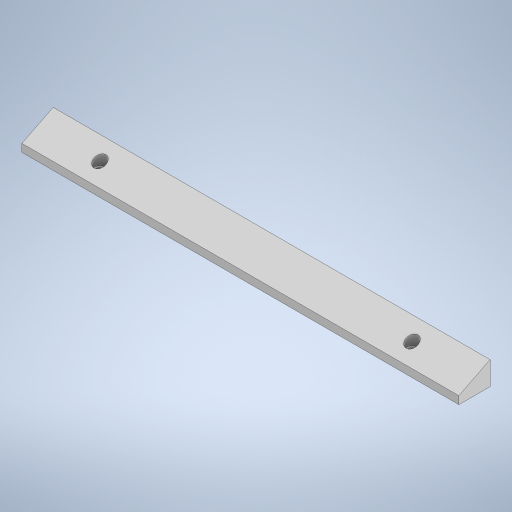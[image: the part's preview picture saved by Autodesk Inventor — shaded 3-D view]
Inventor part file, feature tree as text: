
AUTODESK INVENTOR PART (.ipt)
format: ipt  version: 2023 (Build 270158000, 158)  size: 270,848 bytes
history: native  units: in
note: dims shown in document units (in); Inventor stores cm internally (conversion verified against a paired STEP export)
features: sketch x6, extrude x5
ambient origin geometry x8: Origin, YZ Plane, XZ Plane, XY Plane, X Axis, Y Axis, Z Axis, Center Point
bodies: Solid1 (feature_tree)
feature tree (11):
  extrude  "Extrusion1"  Depth=0.3937in
  extrude  "Extrusion4"  Depth=0.1969in TaperAngle=0.0deg
  sketch  "Sketch7"  dims[d23=0.1772in d24=0.1772in]
  extrude  "Extrusion5"  Depth=0.1772in
  extrude  "Extrusion6"  Depth=0.2953in
  extrude  "Extrusion7"  Depth=0.3937in TaperAngle=0.0deg
  sketch  "Sketch1"  dims[d0=11.0236in d1=0.3937in]
  sketch  "Sketch6"  dims[d2=0.7874in d3=0.0in d21=0.1969in d22=0.0in]
  sketch  "Sketch8"  dims[d25=0.1181in d26=0.0in d27=0.2953in]
  sketch  "Sketch9"  dims[d28=0.2953in d29=0.3937in d30=0.0in]
  sketch  "Sketch10"  dims[d31=0.3937in d32=90.0deg d33=0.0in d34=0.0in d35=7.874in d36=0.3937in d37=0.3937in d38=1.5748in]
